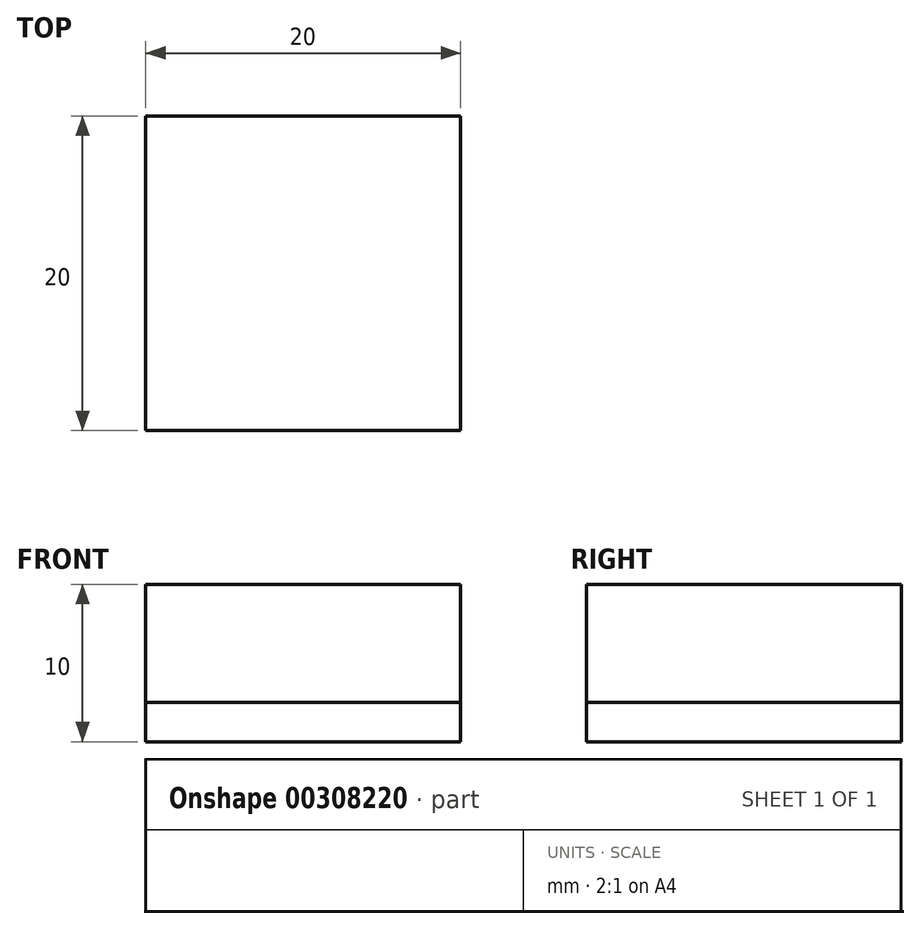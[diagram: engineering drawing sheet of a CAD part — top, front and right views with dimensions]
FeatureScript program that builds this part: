
annotation { "Feature Type Name" : "Feature", "Feature Type Description" : "" }
export const myFeature = defineFeature(function(context is Context, id is Id, definition is map)
    precondition{}
    {
        {
            var Q0;
            Q0=qCreatedBy(makeId("Top.planeOp"),FACE);
            var sketch = newSketch(context, id + "F0", { "sketchPlane" : qUnion([Q0])});
            skLineSegment(sketch, "E0.bottom", {"start": v(10, 10) * mm, "end": v(-10, 10) * mm});
            skLineSegment(sketch, "E0.top", {"start": v(10, -10) * mm, "end": v(-10, -10) * mm});
            skLineSegment(sketch, "E0.left", {"start": v(10, 10) * mm, "end": v(10, -10) * mm});
            skLineSegment(sketch, "E0.right", {"start": v(-10, 10) * mm, "end": v(-10, -10) * mm});
            skPoint(sketch, "E0.middle", {"position": v(0, 0) * mm});
            skSolve(sketch);
        }
        {
            var Q0;
            Q0=makeQuery(id+"F0.imprint","IMPRINT",FACE,{"disambiguationData":[TD([[makeQuery(id+"F0.imprint","IMPRINT",EDGE,{"derivedFrom":sQuery(id+"F0.wireOp",EDGE,"E0.bottom")}),1.0]])]});
            extrude(context, id + "F1", {"entities" : qUnion([Q0]), "depth" : 2.5 * mm, "offsetDistance" : 25 * mm});
        }
        {
            var Q0;
            Q0=makeQuery(id+"F1.opExtrude","CAP_FACE",FACE,{"disambiguationData":[OSD([sQuery(id+"F0.wireOp",EDGE,"E0.bottom"),sQuery(id+"F0.wireOp",EDGE,"E0.top"),sQuery(id+"F0.wireOp",EDGE,"E0.left"),sQuery(id+"F0.wireOp",EDGE,"E0.right")])],"isStart":false});
            extrude(context, id + "F2", {"entities" : qUnion([Q0]), "depth" : 2.5 * mm, "offsetDistance" : 25 * mm});
        }
        {
            var Q0;
            Q0=makeQuery(id+"F2.opExtrude","CAP_FACE",FACE,{"disambiguationData":[OSD([sQuery(id+"F0.wireOp",EDGE,"E0.bottom"),sQuery(id+"F0.wireOp",EDGE,"E0.top"),sQuery(id+"F0.wireOp",EDGE,"E0.left"),sQuery(id+"F0.wireOp",EDGE,"E0.right")])],"isStart":false});
            extrude(context, id + "F3", {"entities" : qUnion([Q0]), "operationType" : NewBodyOperationType.ADD, "depth" : 2.5 * mm, "offsetDistance" : 25 * mm});
        }
        {
            var Q0;
            Q0=makeQuery(id+"F3.opExtrude","CAP_FACE",FACE,{"disambiguationData":[OSD([sQuery(id+"F0.wireOp",EDGE,"E0.bottom"),sQuery(id+"F0.wireOp",EDGE,"E0.top"),sQuery(id+"F0.wireOp",EDGE,"E0.left"),sQuery(id+"F0.wireOp",EDGE,"E0.right")])],"isStart":false});
            extrude(context, id + "F4", {"entities" : qUnion([Q0]), "operationType" : NewBodyOperationType.ADD, "depth" : 2.5 * mm, "offsetDistance" : 25 * mm});
        }
    });
